# Revit family: Washbasins-hansgrohe-61093XXX-Xevolos E Washbasin 600_480 without tap hole and overflow, SmartClean
name_source: partatom
category: Plumbing Fixtures
units: mm (PartAtom-declared; Revit-internal decimal feet)

## family parameters
Always vertical = Yes
Cut with Voids When Loaded = No
OmniClass Number = 23.31.13.00
Part Type = Valve - Breaks Into
Room Calculation Point = No
Round Connector Dimension = Use Diameter
Shared = Yes
Work Plane-Based = No

## types (2) — shared parameters
ARTNR = 61093450
BASENUMBER = 61093
BIMOBJECT = Sanitary: Wash Basins
CATALOG = Hansgrohe
CNSPipeRound/cp_Ausgang_1_V = No
DESIGN = Germany
DO = 46
DOT = 35
ETIM = EC011550 | Washbasin
GTINCODE = 4059625420867
IFC = Sanitary Terminal
L = 600
LI = 370
MASTERFORMAT = 22 41 16.13 | Residential Lavatories
Manufacturer = Hansgrohe
NAME = Xevolos E Washbasin 600/480 without tap hole and overflow, SmartClean
NBSYN = $BASENUMBER.-$ARTNR.-$SURFACE.-$LODLEVEL.
NN = Xevolos Washbasin
OBJECTTYPE = Object (single object)
OMNICLASS = 23-31 13 00 | Sinks
PERMALINK = 61093XXX
PRODUCTFAMILY = Xevolos E
PRODUCTGROUP = Washbasins
PRODUCTURL = https://pro.hansgrohe.com
REGION = Worldwide
SPECIFICATION = Surfaces:  - 61093450 White   Specification:  • consists of: washbasin, waste set, cover  • material: ceramic  • SmartClean: dirt-repellent glaze • degree of gloss: glossy  • ceramic cover included • without tap hole • without overflow • without shelf • non-closing waste set • 600 x 480 mm • type of installation: wall mounted  • suitable for cabinet
SURFACE = GLOSSY_WHITE
TYP = 1
UNICLASS2015 = Pr_40_20_96 | Wash basins, sinks and troughs
UNICLASS_2015_CODE = 40_20_96
UNIFORMATII = D2010 | Plumbing Fixtures
UNSPSC = 301815 | Sanitary ware
WEIGHT = 17
X1 = 280
zero-valued in all types: TAP, X2

## per-type parameters (varying)
| type | LODLEVEL |
| 61093-61093450-GLOSSY_WHITE-200 | 200 |
| 61093-61093450-GLOSSY_WHITE-400 | 400 |

note: column(s) folded — value = type name in every type: LINA, Model, NB

type visibility flags: 2 boolean params named "<type name>_RX0RY0RZ0TX0TY0TZ0_V" — each type sets only its own to Yes (folded from table)

## geometry (parser evidence)
native form markers: Sweep x22
no freeform markers — native parametric forms only
